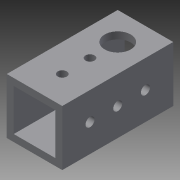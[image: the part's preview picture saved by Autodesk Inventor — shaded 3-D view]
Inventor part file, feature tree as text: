
AUTODESK INVENTOR PART (.ipt)
format: ipt  version: 2014 (Build 180170000, 170)  size: 123,904 bytes
history: native  units: in
note: dims shown in document units (in); Inventor stores cm internally (conversion verified against a paired STEP export)
features: extrude x3, sketch x3
ambient origin geometry x8: Origin, YZ Plane, XZ Plane, XY Plane, X Axis, Y Axis, Z Axis, Center Point
bodies: Solid1 (feature_tree)
feature tree (6):
  extrude  "Extrusion1"  Depth=1.0in
  extrude  "Extrusion2"  Depth=2.0in TaperAngle=0.0deg
  extrude  "Extrusion3"  Depth=2.0in
  sketch  "Sketch1"  dims[d0=1.0in d1=1.0in]
  sketch  "Sketch2"  dims[d2=0.125in d3=2.0in d4=0.0in]
  sketch  "Sketch3"  dims[d5=0.163in d6=0.5in d7=0.5in d8=1.1811in d10=0.5in d11=0.3937in d13=1.0in d15=2.0in d16=0.0in d17=0.163in d18=0.5in d19=0.5in d20=0.7874in d22=0.5in d23=0.3937in d25=1.0in d27=0.4688in d28=0.5in d29=0.5in d30=2.0in d31=0.0in]
